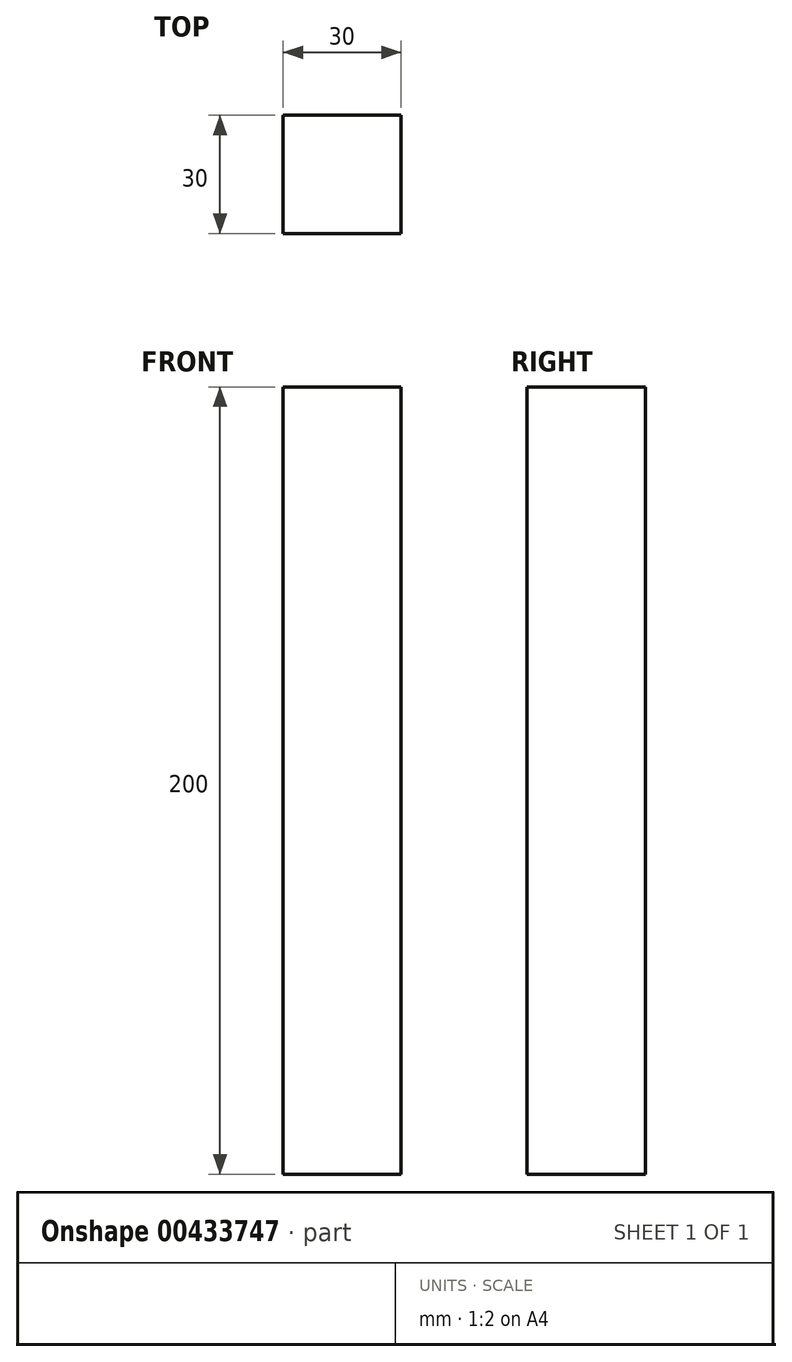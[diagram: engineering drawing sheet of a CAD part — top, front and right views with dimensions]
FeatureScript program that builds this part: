
annotation { "Feature Type Name" : "Feature", "Feature Type Description" : "" }
export const myFeature = defineFeature(function(context is Context, id is Id, definition is map)
    precondition{}
    {
        {
            var Q0;
            Q0=qCreatedBy(makeId("Front.planeOp"),FACE);
            var sketch = newSketch(context, id + "F0", { "sketchPlane" : qUnion([Q0])});
            skLineSegment(sketch, "E0.bottom", {"start": v(25.05, 187.81) * mm, "end": v(55.05, 187.81) * mm});
            skLineSegment(sketch, "E0.top", {"start": v(25.05, -12.19) * mm, "end": v(55.05, -12.19) * mm});
            skLineSegment(sketch, "E0.left", {"start": v(25.05, 187.81) * mm, "end": v(25.05, -12.19) * mm});
            skLineSegment(sketch, "E0.right", {"start": v(55.05, 187.81) * mm, "end": v(55.05, -12.19) * mm});
            skSolve(sketch);
        }
        {
            var Q0;
            Q0=makeQuery(id+"F0.imprint","IMPRINT",FACE,{"disambiguationData":[TD([[makeQuery(id+"F0.imprint","IMPRINT",EDGE,{"derivedFrom":sQuery(id+"F0.wireOp",EDGE,"E0.bottom")}),-1.0]])]});
            extrude(context, id + "F1", {"entities" : qUnion([Q0]), "depth" : 30 * mm, "offsetDistance" : 25 * mm});
        }
    });
